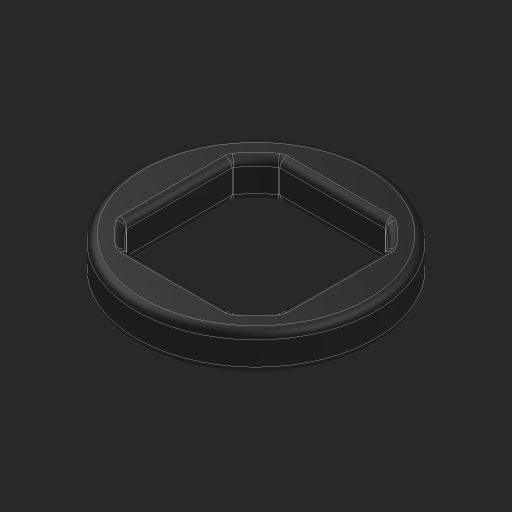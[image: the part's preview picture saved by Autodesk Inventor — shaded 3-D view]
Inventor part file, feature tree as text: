
AUTODESK INVENTOR PART (.ipt)
format: ipt  version: 2023 (Build 270158000, 158)  size: 235,008 bytes
history: native  units: in
note: dims shown in document units (in); Inventor stores cm internally (conversion verified against a paired STEP export)
features: other x5, extrude x1, fillet x1, sketch x1
ambient origin geometry x8: Origin, YZ Plane, XZ Plane, XY Plane, X Axis, Y Axis, Z Axis, Center Point
bodies: Solid1 (feature_tree)
feature tree (8):
  other  "Table"
  other  "HSpacer .0625"
  other  "HSpacer .1250"
  other  "HSpacer .2500"
  other  "HSpacer .5000"
  extrude  "Extrusion1"  Depth=0.0039in
  fillet  "Fillet1"  Radius=0.126in
  sketch  "Sketch1"  dims[d0=0.3937in d2=0.126in d3=0.126in d4=0.3071in d5=0.252in d7=0.0in d8=0.0118in d9=0.0039in]
